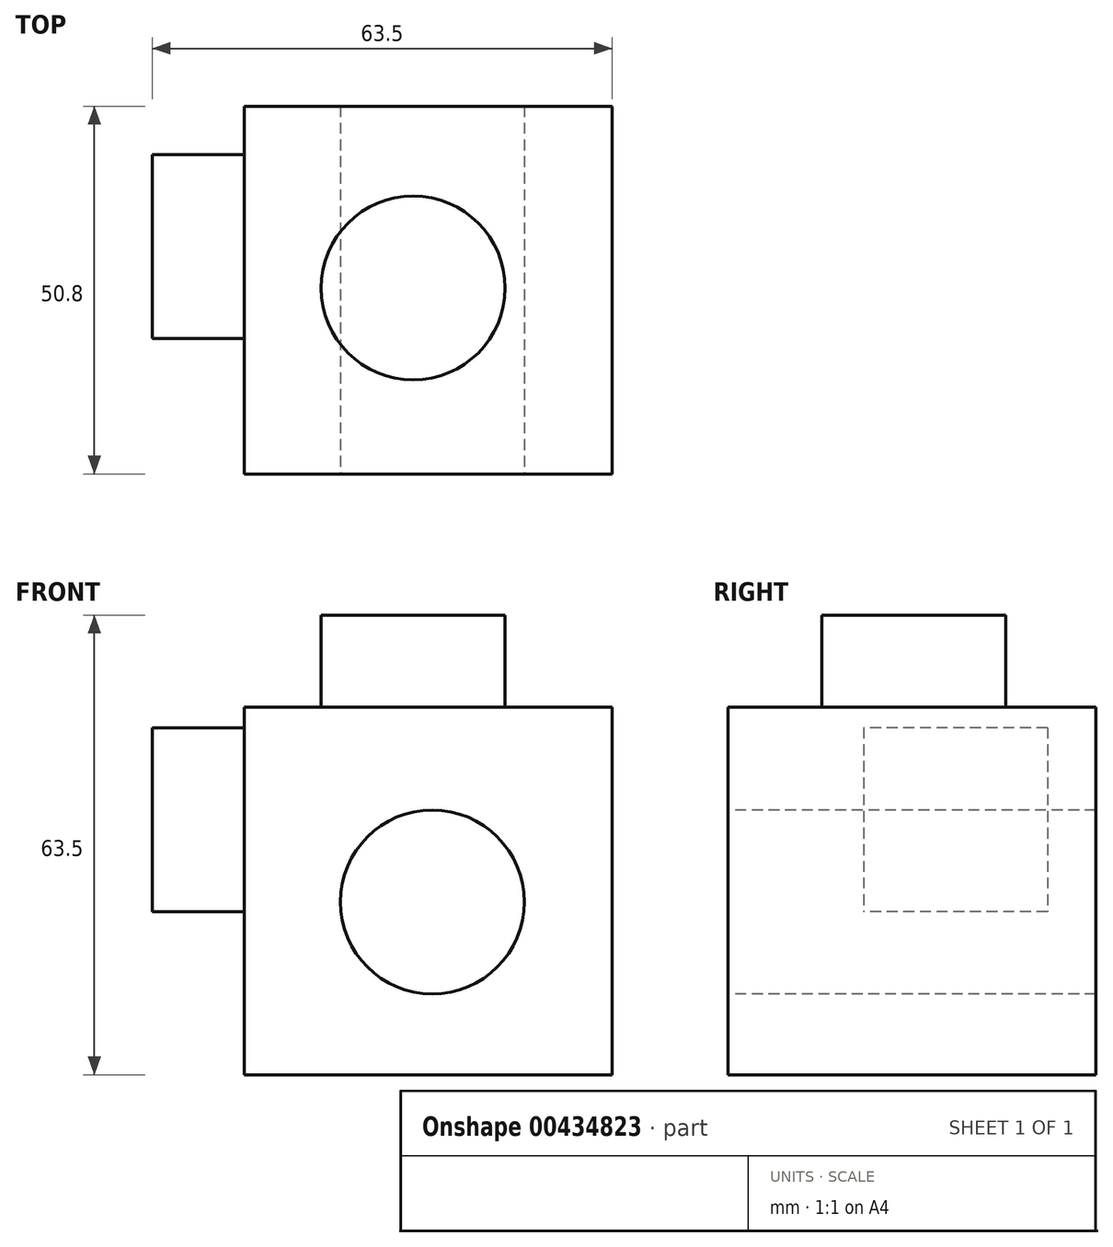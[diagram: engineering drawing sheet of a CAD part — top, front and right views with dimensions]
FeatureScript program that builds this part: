
annotation { "Feature Type Name" : "Feature", "Feature Type Description" : "" }
export const myFeature = defineFeature(function(context is Context, id is Id, definition is map)
    precondition{}
    {
        {
            var Q0;
            Q0=qCreatedBy(makeId("Front.planeOp"),FACE);
            var sketch = newSketch(context, id + "F0", { "sketchPlane" : qUnion([Q0])});
            skLineSegment(sketch, "E0", {"start": v(-44.3, 38.2) * mm, "end": v(6.5, 38.2) * mm});
            skLineSegment(sketch, "E1", {"start": v(-44.3, 38.2) * mm, "end": v(-44.3, -12.6) * mm});
            skLineSegment(sketch, "E2", {"start": v(-44.3, -12.6) * mm, "end": v(6.5, -12.6) * mm});
            skLineSegment(sketch, "E3", {"start": v(6.5, 38.2) * mm, "end": v(6.5, -12.6) * mm});
            skSolve(sketch);
        }
        {
            var Q0;
            Q0 = qSketchRegion(id + "F0", true);
            extrude(context, id + "F1", {"entities" : qUnion([Q0]), "depth" : 50.8 * mm});
        }
        {
            var Q0;
            Q0=makeQuery(id+"F1.opExtrude","CAP_FACE",FACE,{"disambiguationData":[OSD([sQuery(id+"F0.wireOp",EDGE,"E0"),sQuery(id+"F0.wireOp",EDGE,"E1"),sQuery(id+"F0.wireOp",EDGE,"E2"),sQuery(id+"F0.wireOp",EDGE,"E3")])],"isStart":false});
            var sketch = newSketch(context, id + "F2", { "sketchPlane" : qUnion([Q0])});
            skCircle(sketch, "E4", {"center": v(-18.33, 11.27) * mm, "radius": 12.7 * mm});
            skSolve(sketch);
        }
        {
            var Q0;
            Q0 = qSketchRegion(id + "F2", true);
            extrude(context, id + "F3", {"entities" : qUnion([Q0]), "operationType" : NewBodyOperationType.REMOVE, "oppositeDirection" : true, "depth" : 50.8 * mm});
        }
        {
            var Q0;
            Q0=makeQuery(id+"F1.opExtrude","SWEPT_FACE",FACE,{"disambiguationData":[OSD([sQuery(id+"F0.wireOp",EDGE,"E1")])]});
            var sketch = newSketch(context, id + "F4", { "sketchPlane" : qUnion([Q0])});
            skLineSegment(sketch, "E5", {"start": v(6.68, 35.33) * mm, "end": v(32.08, 35.33) * mm});
            skLineSegment(sketch, "E6", {"start": v(6.68, 35.33) * mm, "end": v(6.68, 9.93) * mm});
            skLineSegment(sketch, "E7", {"start": v(6.68, 9.93) * mm, "end": v(32.08, 9.93) * mm});
            skLineSegment(sketch, "E8", {"start": v(32.08, 35.33) * mm, "end": v(32.08, 9.93) * mm});
            skSolve(sketch);
        }
        {
            var Q0;
            Q0 = qSketchRegion(id + "F4", true);
            extrude(context, id + "F5", {"entities" : qUnion([Q0]), "operationType" : NewBodyOperationType.ADD, "depth" : 12.7 * mm});
        }
        {
            var Q0;
            Q0=makeQuery(id+"F1.opExtrude","SWEPT_FACE",FACE,{"disambiguationData":[OSD([sQuery(id+"F0.wireOp",EDGE,"E0")])]});
            var sketch = newSketch(context, id + "F6", { "sketchPlane" : qUnion([Q0])});
            skCircle(sketch, "E9", {"center": v(-20.98, -25.12) * mm, "radius": 12.7 * mm});
            skSolve(sketch);
        }
        {
            var Q0;
            Q0 = qSketchRegion(id + "F6", true);
            extrude(context, id + "F7", {"entities" : qUnion([Q0]), "operationType" : NewBodyOperationType.ADD, "depth" : 12.7 * mm});
        }
    });
